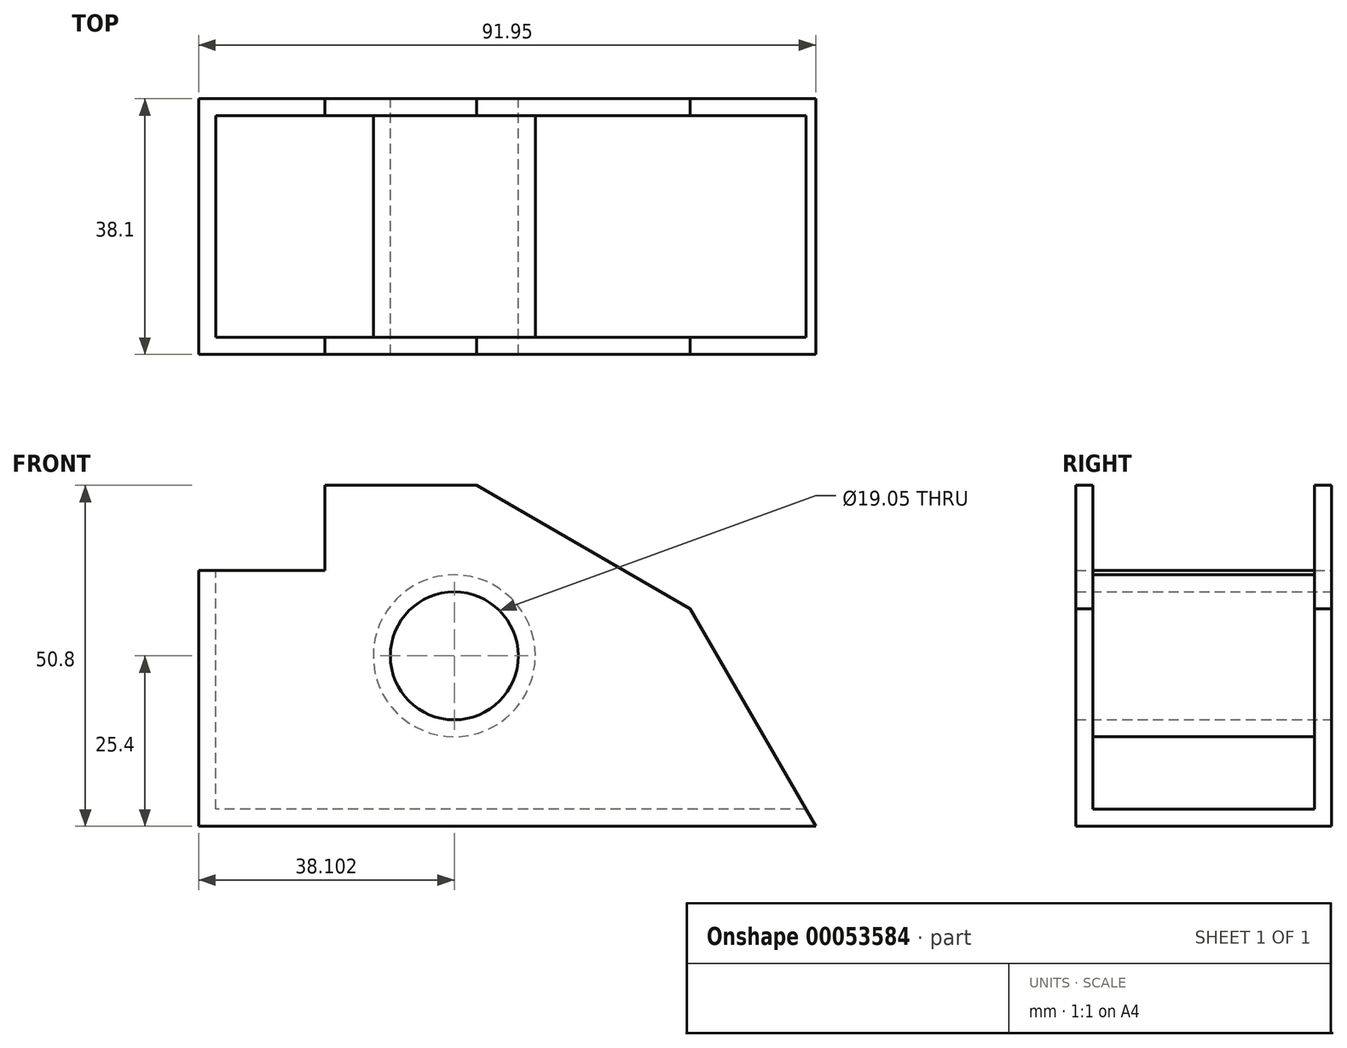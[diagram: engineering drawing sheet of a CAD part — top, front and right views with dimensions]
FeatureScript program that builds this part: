
annotation { "Feature Type Name" : "Feature", "Feature Type Description" : "" }
export const myFeature = defineFeature(function(context is Context, id is Id, definition is map)
    precondition{}
    {
        {
            var Q0;
            Q0=qCreatedBy(makeId("Front.planeOp"),FACE);
            var sketch = newSketch(context, id + "F0", { "sketchPlane" : qUnion([Q0])});
            skLineSegment(sketch, "E0", {"start": v(0, 0) * mm, "end": v(-91.95, 0) * mm});
            skLineSegment(sketch, "E1", {"start": v(-91.95, 0) * mm, "end": v(-91.95, 38.1) * mm});
            skLineSegment(sketch, "E2", {"start": v(-18.72, 32.43) * mm, "end": v(0, 0) * mm});
            skCircle(sketch, "E3", {"center": v(-53.85, 25.4) * mm, "radius": 9.53 * mm});
            skLineSegment(sketch, "E4", {"start": v(-91.95, 38.1) * mm, "end": v(-73.12, 38.1) * mm});
            skLineSegment(sketch, "E5", {"start": v(-73.12, 38.1) * mm, "end": v(-73.12, 50.8) * mm});
            skLineSegment(sketch, "E6", {"start": v(-73.12, 50.8) * mm, "end": v(-50.55, 50.8) * mm});
            skLineSegment(sketch, "E7", {"start": v(-18.72, 32.43) * mm, "end": v(-50.55, 50.8) * mm});
            skLineSegment(sketch, "E8.bottom", {"start": v(0, 0) * mm, "end": v(0, 0) * mm});
            skSolve(sketch);
        }
        {
            var Q0;
            Q0=makeQuery(id+"F0.imprint","IMPRINT",FACE,{"disambiguationData":[TD([[makeQuery(id+"F0.imprint","IMPRINT",EDGE,{"derivedFrom":sQuery(id+"F0.wireOp",EDGE,"E0")}),-1.0]])]});
            extrude(context, id + "F1", {"entities" : qUnion([Q0]), "depth" : 38.1 * mm});
        }
        {
            var Q0;
            Q0=makeQuery(id+"F1.opExtrude","SWEPT_FACE",FACE,{"disambiguationData":[OSD([sQuery(id+"F0.wireOp",EDGE,"E5")])]});
            var Q1;
            Q1=makeQuery(id+"F1.opExtrude","SWEPT_FACE",FACE,{"disambiguationData":[OSD([sQuery(id+"F0.wireOp",EDGE,"E4")])]});
            var Q2;
            Q2=makeQuery(id+"F1.opExtrude","SWEPT_FACE",FACE,{"disambiguationData":[OSD([sQuery(id+"F0.wireOp",EDGE,"E6")])]});
            var Q3;
            Q3=makeQuery(id+"F1.opExtrude","SWEPT_FACE",FACE,{"disambiguationData":[OSD([sQuery(id+"F0.wireOp",EDGE,"E7")])]});
            var Q4;
            Q4=makeQuery(id+"F1.opExtrude","SWEPT_FACE",FACE,{"disambiguationData":[OSD([sQuery(id+"F0.wireOp",EDGE,"E2")])]});
            shell(context, id + "F2", {"entities" : qUnion([Q0, Q1, Q2, Q3, Q4]), "thickness" : 2.54 * mm});
        }
    });
